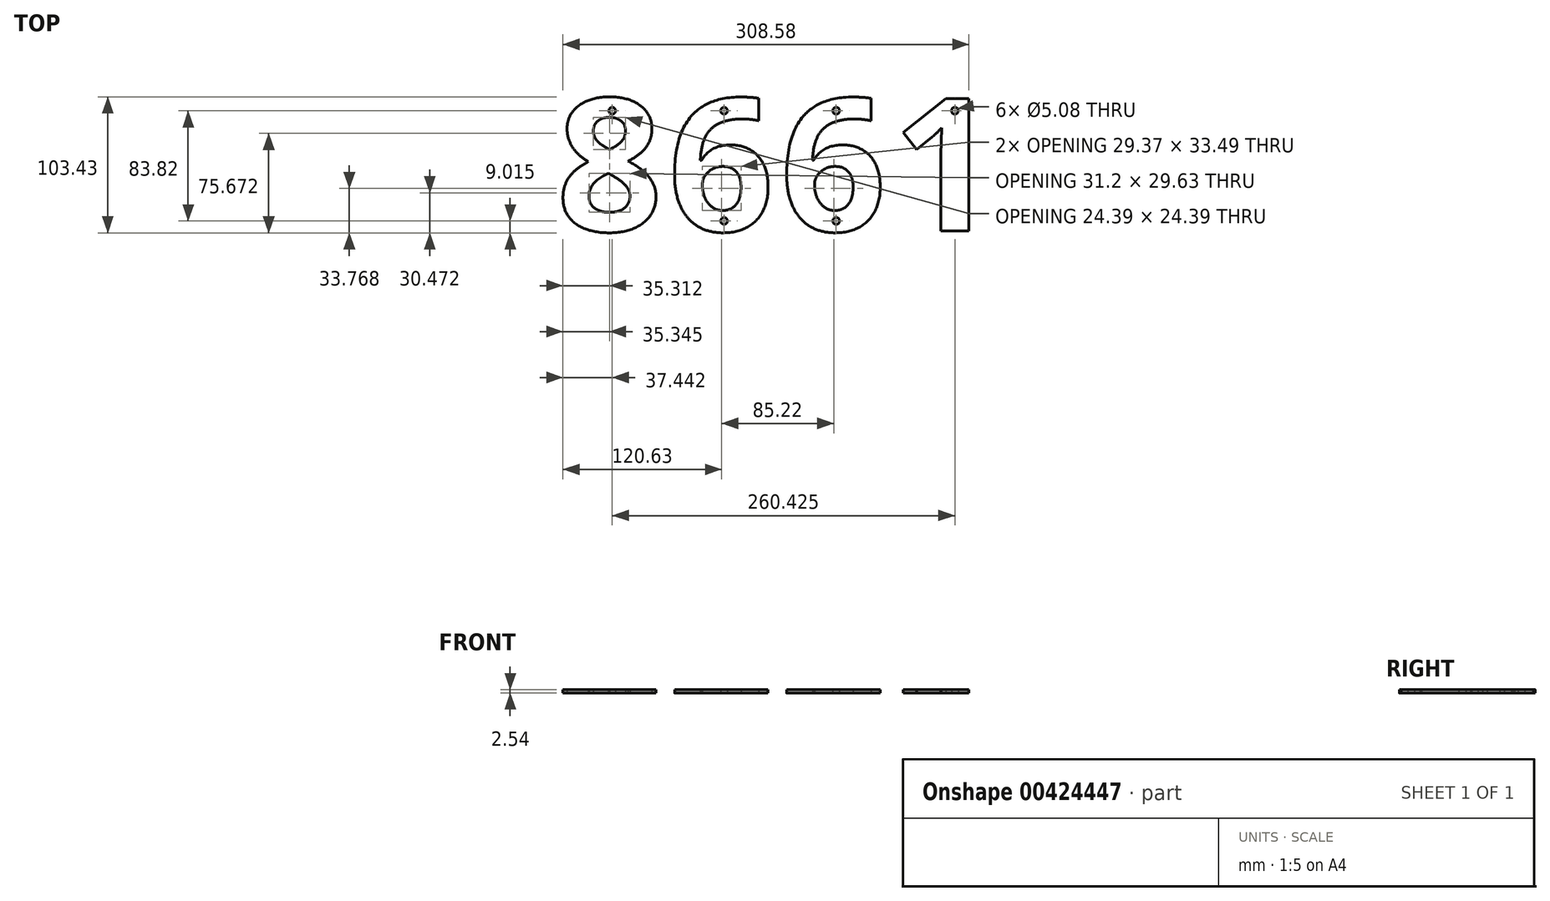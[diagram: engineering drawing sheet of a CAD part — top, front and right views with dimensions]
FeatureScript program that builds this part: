
annotation { "Feature Type Name" : "Feature", "Feature Type Description" : "" }
export const myFeature = defineFeature(function(context is Context, id is Id, definition is map)
    precondition{}
    {
        {
            var Q0;
            Q0=qCreatedBy(makeId("Top.planeOp"),FACE);
            var sketch = newSketch(context, id + "F0", { "sketchPlane" : qUnion([Q0])});
            skText(sketch, "E0", { "text": "8", "fontName": "OpenSans-Bold.ttf"});
            skText(sketch, "E1", { "text": "6", "fontName": "OpenSans-Bold.ttf"});
            skText(sketch, "E2", { "text": "6\n", "fontName": "OpenSans-Bold.ttf"});
            skText(sketch, "E3", { "text": "1\n", "fontName": "OpenSans-Bold.ttf"});
            skLineSegment(sketch, "E4", {"start": v(-153.1, 87.72) * mm, "end": v(169.58, 87.72) * mm});
            skLineSegment(sketch, "E5", {"start": v(-153.1, 3.9) * mm, "end": v(169.58, 3.9) * mm});
            skCircle(sketch, "E6", {"center": v(-110.7, 87.72) * mm, "radius": 2.54 * mm});
            skCircle(sketch, "E7", {"center": v(-25.69, 87.72) * mm, "radius": 2.54 * mm});
            skCircle(sketch, "E8", {"center": v(59.53, 87.72) * mm, "radius": 2.54 * mm});
            skCircle(sketch, "E9", {"center": v(59.53, 3.9) * mm, "radius": 2.54 * mm});
            skCircle(sketch, "E10", {"center": v(-25.69, 3.9) * mm, "radius": 2.54 * mm});
            skCircle(sketch, "E11", {"center": v(149.73, 87.72) * mm, "radius": 2.54 * mm});
            const initialGuessF0  = {"E0": [-0.1531, -0.00372, 1, 0, 0.1016], "E1": [-0.0683, -0.00372, 1, 0, 0.1016], "E2": [0.01692, -0.00372, 1, 0, 0.1016], "E3": [0.10214, -0.00372, 1, 0, 0.1016]};
            skSetInitialGuess(sketch, initialGuessF0);
            skSolve(sketch);
        }
        {
            var Q0;
            {var subQ13=sQuery(id+"F0.wireOp",EDGE,"E0.sketch_text.stroke-2");Q0=makeQuery(id+"F0.imprint","IMPRINT",FACE,{"disambiguationData":[TD([[makeQuery(id+"F0.imprint","IMPRINT",EDGE,{"derivedFrom":subQ13}),-1.0]])]});}
            var Q1;
            {var subQ7=sQuery(id+"F0.wireOp",EDGE,"E0.sketch_text.stroke-0");Q1=makeQuery(id+"F0.imprint","IMPRINT",FACE,{"disambiguationData":[TD([[makeQuery(id+"F0.imprint","IMPRINT",EDGE,{"derivedFrom":subQ7}),-1.0]])]});}
            var Q2;
            {var subQ4=sQuery(id+"F0.wireOp",EDGE,"E0.sketch_text.stroke-7");Q2=makeQuery(id+"F0.imprint","IMPRINT",FACE,{"disambiguationData":[TD([[makeQuery(id+"F0.imprint","IMPRINT",EDGE,{"derivedFrom":subQ4}),-1.0]])]});}
            var Q3;
            {var subQ9=sQuery(id+"F0.wireOp",EDGE,"E1.sketch_text.stroke-0");Q3=makeQuery(id+"F0.imprint","IMPRINT",FACE,{"disambiguationData":[TD([[makeQuery(id+"F0.imprint","IMPRINT",EDGE,{"derivedFrom":subQ9}),-1.0]])]});}
            var Q4;
            {var subQ6=sQuery(id+"F0.wireOp",EDGE,"E1.sketch_text.stroke-2");Q4=makeQuery(id+"F0.imprint","IMPRINT",FACE,{"disambiguationData":[TD([[makeQuery(id+"F0.imprint","IMPRINT",EDGE,{"derivedFrom":subQ6}),-1.0]])]});}
            var Q5;
            {var subQ5=sQuery(id+"F0.wireOp",EDGE,"E1.sketch_text.stroke-14");Q5=makeQuery(id+"F0.imprint","IMPRINT",FACE,{"disambiguationData":[TD([[makeQuery(id+"F0.imprint","IMPRINT",EDGE,{"derivedFrom":subQ5}),-1.0]])]});}
            var Q6;
            {var subQ17=sQuery(id+"F0.wireOp",EDGE,"E2.sketch_text.stroke-0");Q6=makeQuery(id+"F0.imprint","IMPRINT",FACE,{"disambiguationData":[TD([[makeQuery(id+"F0.imprint","IMPRINT",EDGE,{"derivedFrom":subQ17}),-1.0]])]});}
            var Q7;
            {var subQ7=sQuery(id+"F0.wireOp",EDGE,"E2.sketch_text.stroke-2");Q7=makeQuery(id+"F0.imprint","IMPRINT",FACE,{"disambiguationData":[TD([[makeQuery(id+"F0.imprint","IMPRINT",EDGE,{"derivedFrom":subQ7}),-1.0]])]});}
            var Q8;
            {var subQ5=sQuery(id+"F0.wireOp",EDGE,"E2.sketch_text.stroke-14");Q8=makeQuery(id+"F0.imprint","IMPRINT",FACE,{"disambiguationData":[TD([[makeQuery(id+"F0.imprint","IMPRINT",EDGE,{"derivedFrom":subQ5}),-1.0]])]});}
            var Q9;
            {var subQ11=sQuery(id+"F0.wireOp",EDGE,"E3.sketch_text.stroke-2");Q9=makeQuery(id+"F0.imprint","IMPRINT",FACE,{"disambiguationData":[TD([[makeQuery(id+"F0.imprint","IMPRINT",EDGE,{"derivedFrom":subQ11}),-1.0]])]});}
            var Q10;
            {var subQ6=sQuery(id+"F0.wireOp",EDGE,"E3.sketch_text.stroke-8");Q10=makeQuery(id+"F0.imprint","IMPRINT",FACE,{"disambiguationData":[TD([[makeQuery(id+"F0.imprint","IMPRINT",EDGE,{"derivedFrom":subQ6}),-1.0]])]});}
            var Q11;
            {var subQ0=sQuery(id+"F0.wireOp",EDGE,"E3.sketch_text.stroke-0");Q11=makeQuery(id+"F0.imprint","IMPRINT",FACE,{"disambiguationData":[TD([[makeQuery(id+"F0.imprint","IMPRINT",EDGE,{"derivedFrom":subQ0}),-1.0]])]});}
            extrude(context, id + "F1", {"entities" : qUnion([Q0, Q1, Q2, Q3, Q4, Q5, Q6, Q7, Q8, Q9, Q10, Q11]), "depth" : 2.54 * mm});
        }
    });
